# Revit family: CENTUM Spannschloss DIN1480 geschmiedet M16
name_source: partatom
category: HLS-Bauteile
revit_build: Autodesk Revit 2017 (Build: 20190507_1515(x64)
units: mm (PartAtom-declared; Revit-internal decimal feet)

## family parameters
Arbeitsebenenbasiert = Ja
Beim Laden mit Abzugskörper schneiden = Nein
Bemaßung runder Anschluss = Durchmesser verwenden
Gemeinsam genutzt = Ja
Immer vertikal = Nein
Raumberechnungspunkt = Nein
Teiletyp = Normal

## types (1)
- CENTUM Spannschloss DIN1480 geschmiedet M16
    Artikelnummer = 1660007456
    Außendurchmesser = 42 mm  [stored 0.137795 ft]
    EAN = 4250928449580
    Fabrikat = MEFA
    Firma = MEFA Befestigungs- und Montagesysteme GmbH
    Gewicht = 0.51 kg
    Gewicht pro Bauteil = 0.51 kg
    Gewinde = M16
    Kurztext1 = Spannschloss offen DIN 1480
    Kurztext2 = M16 fsv
    Länge = 170 mm  [stored 0.557743 ft]
    Material = Stahl
    Mengeneinheit = St
    Nachstellbarkeit = 110 mm
    Oberflaeche = feuerstückverzinkt
    Vorgabe-Ansicht = 1219 mm
    max. zul. Last = 11.20 kN
    vpe = 1 St

note: [stored X ft] marks values corroborated as IEEE doubles in the binary element streams (Revit-internal decimal feet)
